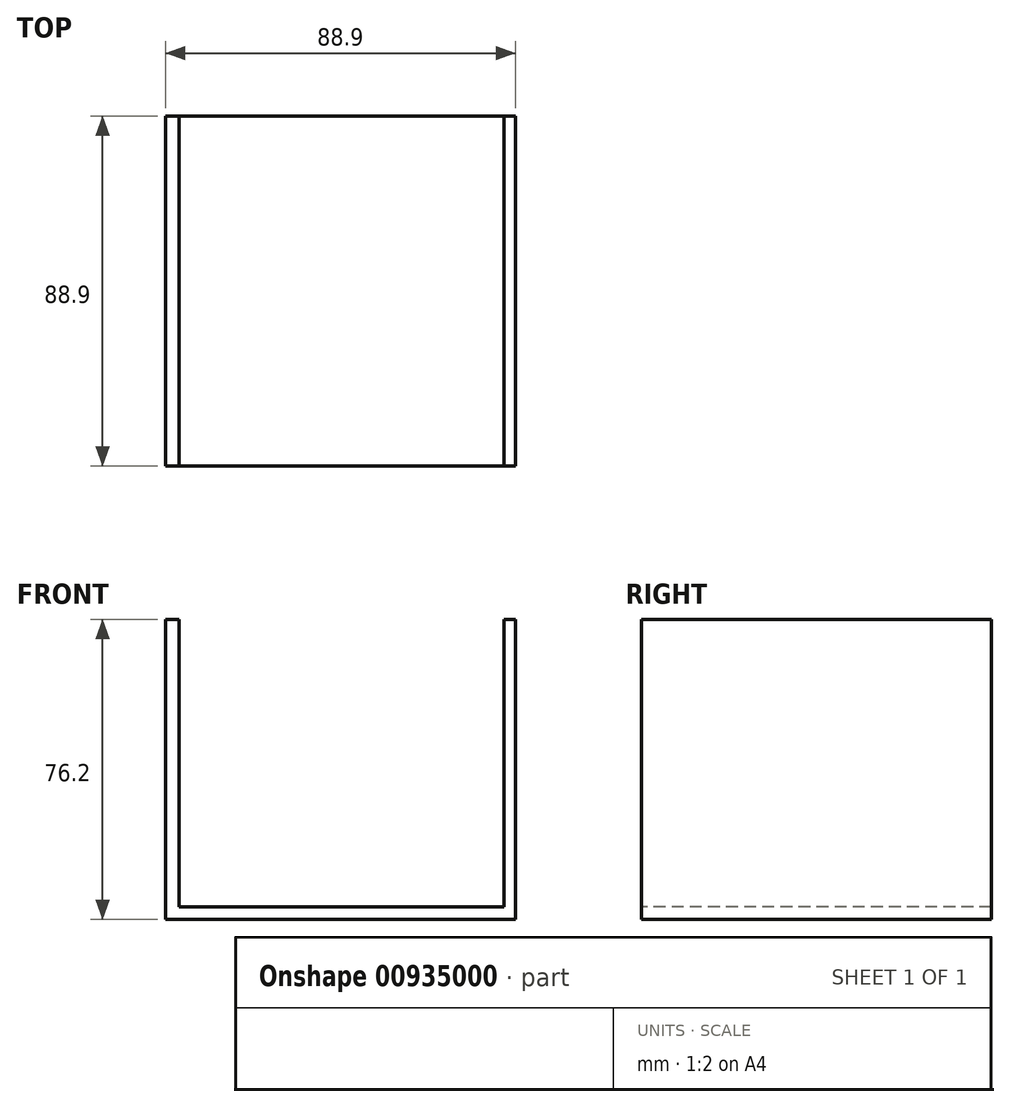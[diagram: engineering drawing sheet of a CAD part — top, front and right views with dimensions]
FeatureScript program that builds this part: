
annotation { "Feature Type Name" : "Feature", "Feature Type Description" : "" }
export const myFeature = defineFeature(function(context is Context, id is Id, definition is map)
    precondition{}
    {
        {
            var Q0;
            Q0=qCreatedBy(makeId("Front.planeOp"),FACE);
            var sketch = newSketch(context, id + "F0", { "sketchPlane" : qUnion([Q0])});
            skLineSegment(sketch, "E0.bottom", {"start": v(44.45, -38.1) * mm, "end": v(-44.45, -38.1) * mm});
            skLineSegment(sketch, "E0.top", {"start": v(44.45, 38.1) * mm, "end": v(-44.45, 38.1) * mm});
            skLineSegment(sketch, "E0.left", {"start": v(44.45, -38.1) * mm, "end": v(44.45, 38.1) * mm});
            skLineSegment(sketch, "E0.right", {"start": v(-44.45, -38.1) * mm, "end": v(-44.45, 38.1) * mm});
            skPoint(sketch, "E0.middle", {"position": v(0, 0) * mm});
            skSolve(sketch);
        }
        {
            var Q0;
            Q0 = qSketchRegion(id + "F0", true);
            extrude(context, id + "F1", {"entities" : qUnion([Q0]), "depth" : 88.9 * mm, "offsetDistance" : 25.4 * mm, "symmetric" : true});
        }
        {
            var Q0;
            Q0=qCreatedBy(makeId("Front.planeOp"),FACE);
            var sketch = newSketch(context, id + "F2", { "sketchPlane" : qUnion([Q0])});
            skLineSegment(sketch, "E1.bottom", {"start": v(-40.98, 38.1) * mm, "end": v(41.57, 38.1) * mm});
            skLineSegment(sketch, "E1.top", {"start": v(-40.98, -34.92) * mm, "end": v(41.57, -34.92) * mm});
            skLineSegment(sketch, "E1.left", {"start": v(-40.98, 38.1) * mm, "end": v(-40.98, -34.92) * mm});
            skLineSegment(sketch, "E1.right", {"start": v(41.57, 38.1) * mm, "end": v(41.57, -34.92) * mm});
            skSolve(sketch);
        }
        {
            var Q0;
            Q0 = qSketchRegion(id + "F2", true);
            extrude(context, id + "F3", {"entities" : qUnion([Q0]), "operationType" : NewBodyOperationType.REMOVE, "oppositeDirection" : true, "depth" : 88.9 * mm, "offsetDistance" : 25.4 * mm, "symmetric" : true});
        }
    });
